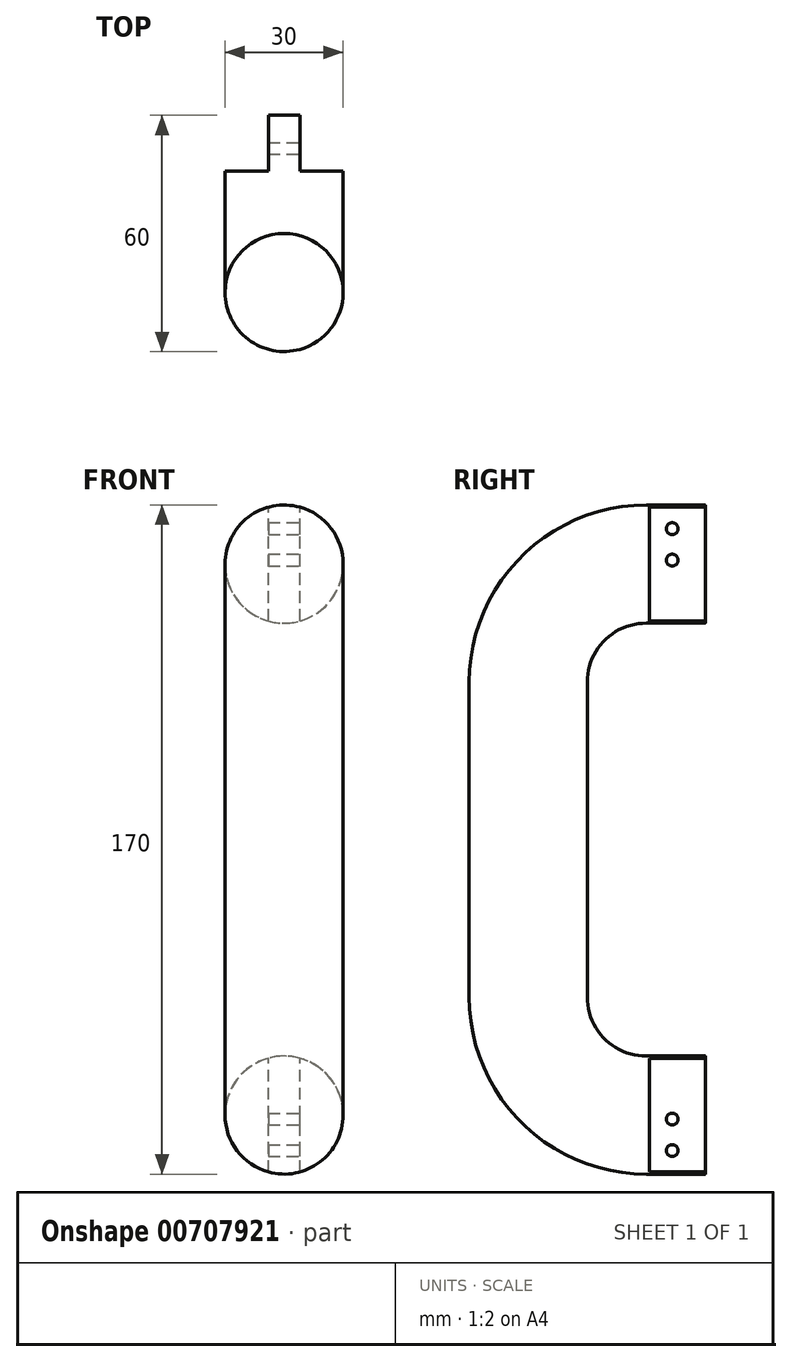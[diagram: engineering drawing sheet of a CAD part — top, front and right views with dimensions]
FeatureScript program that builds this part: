
annotation { "Feature Type Name" : "Feature", "Feature Type Description" : "" }
export const myFeature = defineFeature(function(context is Context, id is Id, definition is map)
    precondition{}
    {
        {
            var Q0;
            Q0=qCreatedBy(makeId("Right.planeOp"),FACE);
            var sketch = newSketch(context, id + "F0", { "sketchPlane" : qUnion([Q0])});
            skLineSegment(sketch, "E0.bottom", {"start": v(15, 85) * mm, "end": v(30, 85) * mm});
            skLineSegment(sketch, "E0.top", {"start": v(15, -85) * mm, "end": v(30, -85) * mm});
            skLineSegment(sketch, "E0.left", {"start": v(-30, 40) * mm, "end": v(-30, -40) * mm});
            skLineSegment(sketch, "E0.right", {"start": v(30, 85) * mm, "end": v(30, 55) * mm});
            skLineSegment(sketch, "E1.bottom", {"start": v(30, 55) * mm, "end": v(15, 55) * mm});
            skLineSegment(sketch, "E1.top", {"start": v(30, -55) * mm, "end": v(15, -55) * mm});
            skLineSegment(sketch, "E1.right", {"start": v(0, 40) * mm, "end": v(0, -40) * mm});
            skLineSegment(sketch, "E2.trimOffspring", {"start": v(30, -55) * mm, "end": v(30, -85) * mm});
            skArc(sketch, "E3.filletArc", {"start": v(0, -40) * mm, "mid": v(4.4, -50.6) * mm, "end": v(15, -55) * mm});
            skArc(sketch, "E4.filletArc", {"start": v(-30, -40) * mm, "mid": v(-16.82, -71.82) * mm, "end": v(15, -85) * mm});
            skArc(sketch, "E5.filletArc", {"start": v(15, 85) * mm, "mid": v(-16.82, 71.82) * mm, "end": v(-30, 40) * mm});
            skPoint(sketch, "E6.visualSharp", {"position": v(0, 55) * mm});
            skArc(sketch, "E6.filletArc", {"start": v(15, 55) * mm, "mid": v(4.4, 50.6) * mm, "end": v(0, 40) * mm});
            skSolve(sketch);
        }
        {
            var Q0;
            Q0 = qSketchRegion(id + "F0", true);
            extrude(context, id + "F1", {"entities" : qUnion([Q0]), "endBound" : BoundingType.SYMMETRIC, "depth" : 30 * mm, "offsetDistance" : 25 * mm});
        }
        {
            var Q0;
            Q0=makeQuery(id+"F1.opExtrude","SWEPT_FACE",FACE,{"disambiguationData":[OSD([sQuery(id+"F0.wireOp",EDGE,"E0.bottom")])]});
            var sketch = newSketch(context, id + "F2", { "sketchPlane" : qUnion([Q0])});
            skLineSegment(sketch, "E7.bottom", {"start": v(-15, 30) * mm, "end": v(-4, 30) * mm});
            skLineSegment(sketch, "E7.top", {"start": v(-15, 15.8) * mm, "end": v(-4, 15.8) * mm});
            skLineSegment(sketch, "E7.left", {"start": v(-15, 30) * mm, "end": v(-15, 15.8) * mm});
            skLineSegment(sketch, "E7.right", {"start": v(-4, 30) * mm, "end": v(-4, 15.8) * mm});
            skLineSegment(sketch, "E8.bottom", {"start": v(4, 30) * mm, "end": v(15, 30) * mm});
            skLineSegment(sketch, "E8.top", {"start": v(4, 15.8) * mm, "end": v(15, 15.8) * mm});
            skLineSegment(sketch, "E8.left", {"start": v(4, 30) * mm, "end": v(4, 15.8) * mm});
            skLineSegment(sketch, "E8.right", {"start": v(15, 30) * mm, "end": v(15, 15.8) * mm});
            skSolve(sketch);
        }
        {
            var Q0;
            Q0 = qSketchRegion(id + "F2", true);
            extrude(context, id + "F3", {"entities" : qUnion([Q0]), "operationType" : NewBodyOperationType.REMOVE, "oppositeDirection" : true, "depth" : 250 * mm, "offsetDistance" : 25 * mm});
        }
        {
            var Q0;
            Q0=makeQuery(id+"F3.boolean.opBoolean","COPY",FACE,{"disambiguationData":[TD([makeQuery(id+"F1.opExtrude","SWEPT_FACE",FACE,{"disambiguationData":[OSD([sQuery(id+"F0.wireOp",EDGE,"E0.bottom")])]})])],"derivedFrom":makeQuery(id+"F3.opExtrude","SWEPT_FACE",FACE,{"disambiguationData":[OSD([sQuery(id+"F2.wireOp",EDGE,"E8.left")])]})});
            var sketch = newSketch(context, id + "F4", { "sketchPlane" : qUnion([Q0])});
            skCircle(sketch, "E9", {"center": v(21.6, 79) * mm, "radius": 1.5 * mm});
            skCircle(sketch, "E10", {"center": v(21.6, 71) * mm, "radius": 1.5 * mm});
            skCircle(sketch, "E11", {"center": v(21.6, -71) * mm, "radius": 1.5 * mm});
            skCircle(sketch, "E12", {"center": v(21.6, -79) * mm, "radius": 1.5 * mm});
            skSolve(sketch);
        }
        {
            var Q0;
            Q0 = qSketchRegion(id + "F4", true);
            extrude(context, id + "F5", {"entities" : qUnion([Q0]), "operationType" : NewBodyOperationType.REMOVE, "oppositeDirection" : true, "depth" : 25 * mm, "offsetDistance" : 25 * mm});
        }
        {
            var Q0;
            Q0=makeQuery(id+"F1.opExtrude","CAP_EDGE",EDGE,{"disambiguationData":[OSD([sQuery(id+"F0.wireOp",EDGE,"E0.bottom")])],"isStart":false});
            var Q1;
            Q1=makeQuery(id+"F1.opExtrude","CAP_EDGE",EDGE,{"disambiguationData":[OSD([sQuery(id+"F0.wireOp",EDGE,"E1.bottom")])],"isStart":false});
            var Q2;
            Q2=makeQuery(id+"F1.opExtrude","CAP_EDGE",EDGE,{"disambiguationData":[OSD([sQuery(id+"F0.wireOp",EDGE,"E0.bottom")])],"isStart":true});
            var Q3;
            Q3=makeQuery(id+"F1.opExtrude","CAP_EDGE",EDGE,{"disambiguationData":[OSD([sQuery(id+"F0.wireOp",EDGE,"E1.bottom")])],"isStart":true});
            fillet(context, id + "F6", {"entities" : qUnion([Q0, Q1, Q2, Q3]), "radius" : 15 * mm, "tangentPropagation" : true, "allowEdgeOverflow" : false});
        }
    });
